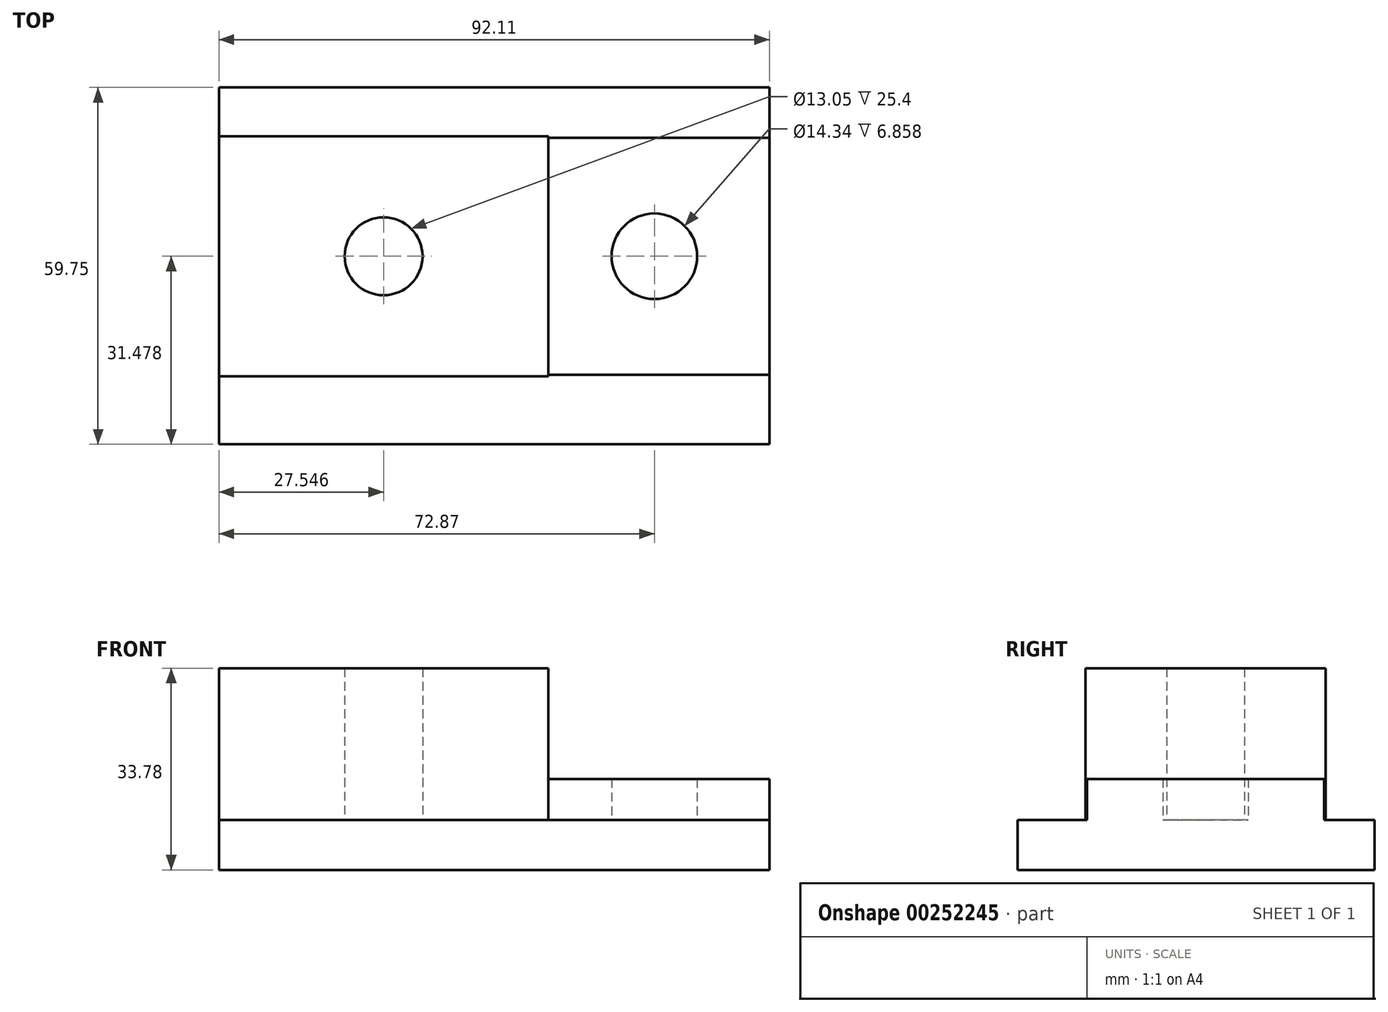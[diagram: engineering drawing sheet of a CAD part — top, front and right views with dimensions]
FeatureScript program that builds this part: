
annotation { "Feature Type Name" : "Feature", "Feature Type Description" : "" }
export const myFeature = defineFeature(function(context is Context, id is Id, definition is map)
    precondition{}
    {
        {
            var Q0;
            Q0=qCreatedBy(makeId("Top.planeOp"),FACE);
            var sketch = newSketch(context, id + "F0", { "sketchPlane" : qUnion([Q0])});
            skLineSegment(sketch, "E0.bottom", {"start": v(-55.09, 26.67) * mm, "end": v(0, 26.67) * mm});
            skLineSegment(sketch, "E0.top", {"start": v(-55.09, -13.55) * mm, "end": v(0, -13.55) * mm});
            skLineSegment(sketch, "E0.left", {"start": v(-55.09, 26.67) * mm, "end": v(-55.09, -13.55) * mm});
            skLineSegment(sketch, "E0.right", {"start": v(0, 26.67) * mm, "end": v(0, -13.55) * mm});
            skCircle(sketch, "E1", {"center": v(-27.54, 6.56) * mm, "radius": 6.53 * mm});
            skPoint(sketch, "E1.centerSnap0", {"position": v(-55.09, 6.56) * mm});
            skPoint(sketch, "E1.centerSnap1", {"position": v(-27.54, 26.67) * mm});
            skSolve(sketch);
        }
        {
            var Q0;
            Q0 = qSketchRegion(id + "F0", true);
            extrude(context, id + "F1", {"entities" : qUnion([Q0]), "depth" : 25.4 * mm});
        }
        {
            var Q0;
            Q0=qCreatedBy(makeId("Top.planeOp"),FACE);
            var sketch = newSketch(context, id + "F2", { "sketchPlane" : qUnion([Q0])});
            skLineSegment(sketch, "E2.bottom", {"start": v(0, 26.38) * mm, "end": v(37.02, 26.38) * mm});
            skLineSegment(sketch, "E2.top", {"start": v(0, -13.26) * mm, "end": v(37.02, -13.26) * mm});
            skLineSegment(sketch, "E2.left", {"start": v(0, 26.38) * mm, "end": v(0, -13.26) * mm});
            skLineSegment(sketch, "E2.right", {"start": v(37.02, 26.38) * mm, "end": v(37.02, -13.26) * mm});
            skCircle(sketch, "E3", {"center": v(17.78, 6.56) * mm, "radius": 7.17 * mm});
            skSolve(sketch);
        }
        {
            var Q0;
            Q0 = qSketchRegion(id + "F2", true);
            extrude(context, id + "F3", {"entities" : qUnion([Q0]), "operationType" : NewBodyOperationType.ADD, "depth" : 6.86 * mm});
        }
        {
            var Q0;
            Q0=makeQuery(id+"F3.boolean.opBoolean","MERGE",FACE,{"derivedFrom":[makeQuery(id+"F1.opExtrude","CAP_FACE",FACE,{"disambiguationData":[OSD([sQuery(id+"F0.wireOp",EDGE,"E0.bottom"),sQuery(id+"F0.wireOp",EDGE,"E0.top"),sQuery(id+"F0.wireOp",EDGE,"E0.left"),sQuery(id+"F0.wireOp",EDGE,"E0.right"),sQuery(id+"F0.wireOp",EDGE,"E1")])],"isStart":true}),makeQuery(id+"F3.opExtrude","CAP_FACE",FACE,{"disambiguationData":[OSD([sQuery(id+"F2.wireOp",EDGE,"E2.bottom"),sQuery(id+"F2.wireOp",EDGE,"E2.top"),sQuery(id+"F2.wireOp",EDGE,"E2.left"),sQuery(id+"F2.wireOp",EDGE,"E2.right"),sQuery(id+"F2.wireOp",EDGE,"E3")])],"isStart":true})]});
            var sketch = newSketch(context, id + "F4", { "sketchPlane" : qUnion([Q0])});
            skLineSegment(sketch, "E4.bottom", {"start": v(-55.09, 24.92) * mm, "end": v(37.02, 24.92) * mm});
            skLineSegment(sketch, "E4.top", {"start": v(-55.09, -34.83) * mm, "end": v(37.02, -34.83) * mm});
            skLineSegment(sketch, "E4.left", {"start": v(-55.09, 24.92) * mm, "end": v(-55.09, -34.83) * mm});
            skLineSegment(sketch, "E4.right", {"start": v(37.02, 24.92) * mm, "end": v(37.02, -34.83) * mm});
            skSolve(sketch);
        }
        {
            var Q0;
            Q0 = qSketchRegion(id + "F4", true);
            extrude(context, id + "F5", {"entities" : qUnion([Q0]), "operationType" : NewBodyOperationType.ADD, "depth" : 8.38 * mm});
        }
    });
